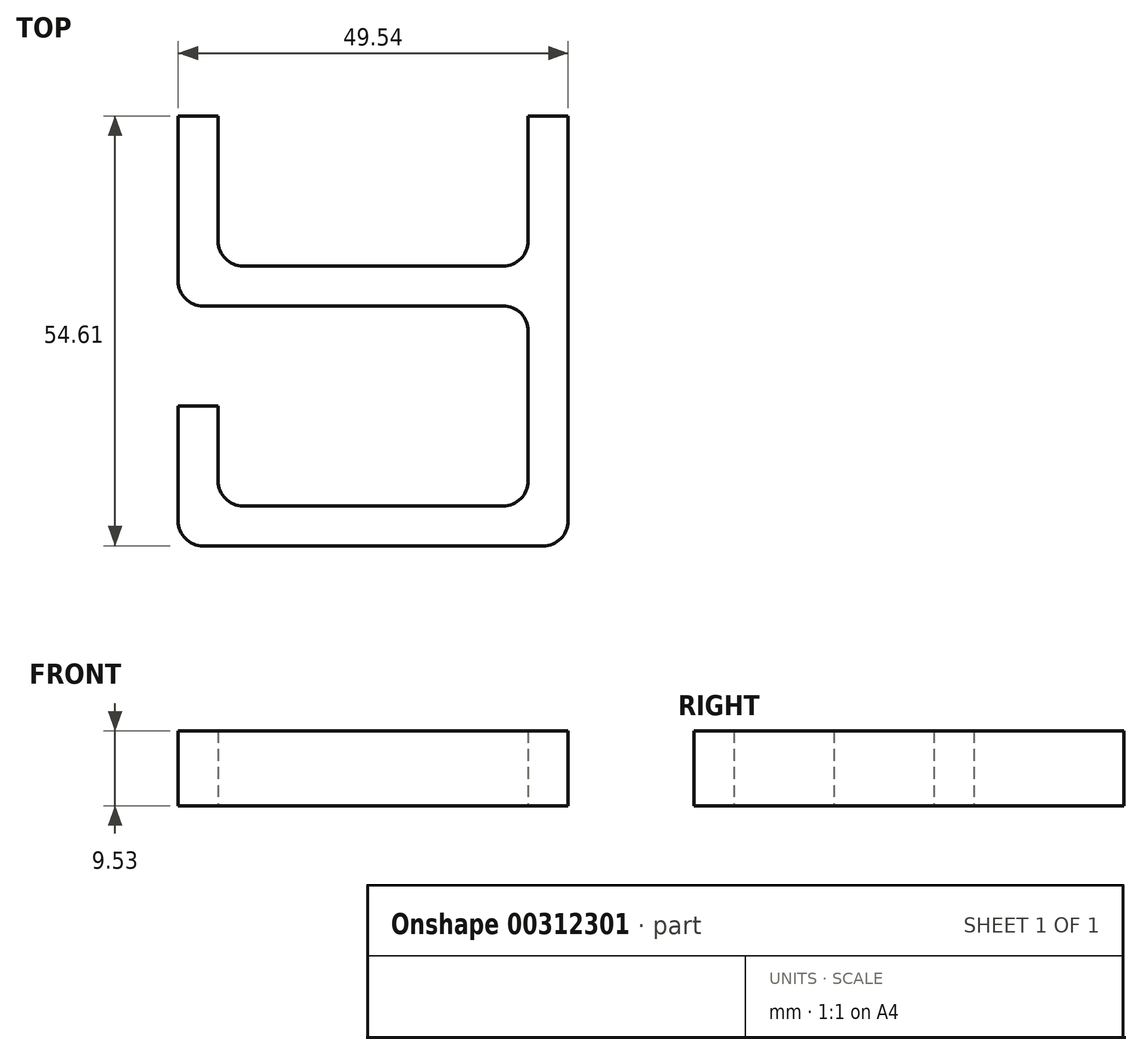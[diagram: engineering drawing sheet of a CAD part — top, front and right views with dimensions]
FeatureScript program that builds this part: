
annotation { "Feature Type Name" : "Feature", "Feature Type Description" : "" }
export const myFeature = defineFeature(function(context is Context, id is Id, definition is map)
    precondition{}
    {
        {
            var Q0;
            Q0=qCreatedBy(makeId("Top.planeOp"),FACE);
            var sketch = newSketch(context, id + "F0", { "sketchPlane" : qUnion([Q0])});
            skLineSegment(sketch, "E0.bottom", {"start": v(19.69, 25.4) * mm, "end": v(-19.68, 25.4) * mm, "construction": true});
            skLineSegment(sketch, "E0.top", {"start": v(16.51, -25.4) * mm, "end": v(-16.5, -25.4) * mm});
            skLineSegment(sketch, "E0.left", {"start": v(19.69, -6.35) * mm, "end": v(19.69, -22.23) * mm});
            skLineSegment(sketch, "E0.right", {"start": v(-19.68, -6.35) * mm, "end": v(-19.68, -22.23) * mm});
            skPoint(sketch, "E0.middle", {"position": v(0, 0) * mm});
            skLineSegment(sketch, "E1.top", {"start": v(21.59, -60.96) * mm, "end": v(-21.59, -60.96) * mm});
            skLineSegment(sketch, "E1.left", {"start": v(24.77, -6.35) * mm, "end": v(24.77, -57.79) * mm});
            skLineSegment(sketch, "E1.right", {"start": v(-24.77, -6.35) * mm, "end": v(-24.77, -27.3) * mm});
            skPoint(sketch, "E1.middle", {"position": v(0, -30.48) * mm});
            skLineSegment(sketch, "E2.bottom", {"start": v(-21.59, -30.48) * mm, "end": v(16.5, -30.48) * mm});
            skLineSegment(sketch, "E2.top", {"start": v(-16.51, -55.88) * mm, "end": v(16.51, -55.88) * mm});
            skLineSegment(sketch, "E2.left", {"start": v(-24.77, -43.18) * mm, "end": v(-24.77, -55.88) * mm});
            skLineSegment(sketch, "E2.right", {"start": v(19.68, -33.66) * mm, "end": v(19.68, -52.7) * mm});
            skLineSegment(sketch, "E3", {"start": v(-24.77, -43.18) * mm, "end": v(-19.69, -43.18) * mm});
            skLineSegment(sketch, "E4", {"start": v(-19.68, -43.18) * mm, "end": v(-19.68, -52.7) * mm});
            skLineSegment(sketch, "E5.trimOffspring", {"start": v(-24.77, -43.18) * mm, "end": v(-24.77, -57.79) * mm});
            skLineSegment(sketch, "E6", {"start": v(-24.77, -6.35) * mm, "end": v(-19.68, -6.35) * mm});
            skPoint(sketch, "E7.trimOffspring.end.orphan", {"position": v(-24.77, 0) * mm});
            skLineSegment(sketch, "E8.trimOffspring", {"start": v(19.69, -6.35) * mm, "end": v(24.77, -6.35) * mm});
            skPoint(sketch, "E9.orphan", {"position": v(24.77, 0) * mm});
            skPoint(sketch, "E10.visualSharp", {"position": v(-19.69, -55.88) * mm});
            skArc(sketch, "E10.filletArc", {"start": v(-19.69, -52.7) * mm, "mid": v(-18.76, -54.95) * mm, "end": v(-16.51, -55.88) * mm});
            skPoint(sketch, "E11.visualSharp", {"position": v(-24.77, -60.96) * mm});
            skArc(sketch, "E11.filletArc", {"start": v(-24.77, -57.79) * mm, "mid": v(-23.84, -60.03) * mm, "end": v(-21.59, -60.96) * mm});
            skPoint(sketch, "E12.visualSharp", {"position": v(19.69, -55.88) * mm});
            skArc(sketch, "E12.filletArc", {"start": v(16.51, -55.88) * mm, "mid": v(18.76, -54.95) * mm, "end": v(19.69, -52.7) * mm});
            skPoint(sketch, "E13.visualSharp", {"position": v(19.69, -25.4) * mm});
            skArc(sketch, "E13.filletArc", {"start": v(16.51, -25.4) * mm, "mid": v(18.76, -24.47) * mm, "end": v(19.69, -22.23) * mm});
            skPoint(sketch, "E14.visualSharp", {"position": v(-19.68, -25.4) * mm});
            skArc(sketch, "E14.filletArc", {"start": v(-19.68, -22.23) * mm, "mid": v(-18.76, -24.47) * mm, "end": v(-16.5, -25.4) * mm});
            skPoint(sketch, "E15.visualSharp", {"position": v(24.77, -60.96) * mm});
            skArc(sketch, "E15.filletArc", {"start": v(21.59, -60.96) * mm, "mid": v(23.84, -60.03) * mm, "end": v(24.77, -57.79) * mm});
            skPoint(sketch, "E16.visualSharp", {"position": v(-24.77, -30.48) * mm});
            skArc(sketch, "E16.filletArc", {"start": v(-24.77, -27.3) * mm, "mid": v(-23.84, -29.55) * mm, "end": v(-21.59, -30.48) * mm});
            skPoint(sketch, "E17.visualSharp", {"position": v(19.69, -30.48) * mm});
            skArc(sketch, "E17.filletArc", {"start": v(19.68, -33.66) * mm, "mid": v(18.76, -31.4) * mm, "end": v(16.5, -30.48) * mm});
            skSolve(sketch);
        }
        {
            var Q0;
            Q0 = qSketchRegion(id + "F0", true);
            extrude(context, id + "F1", {"entities" : qUnion([Q0]), "depth" : 9.52 * mm});
        }
    });
